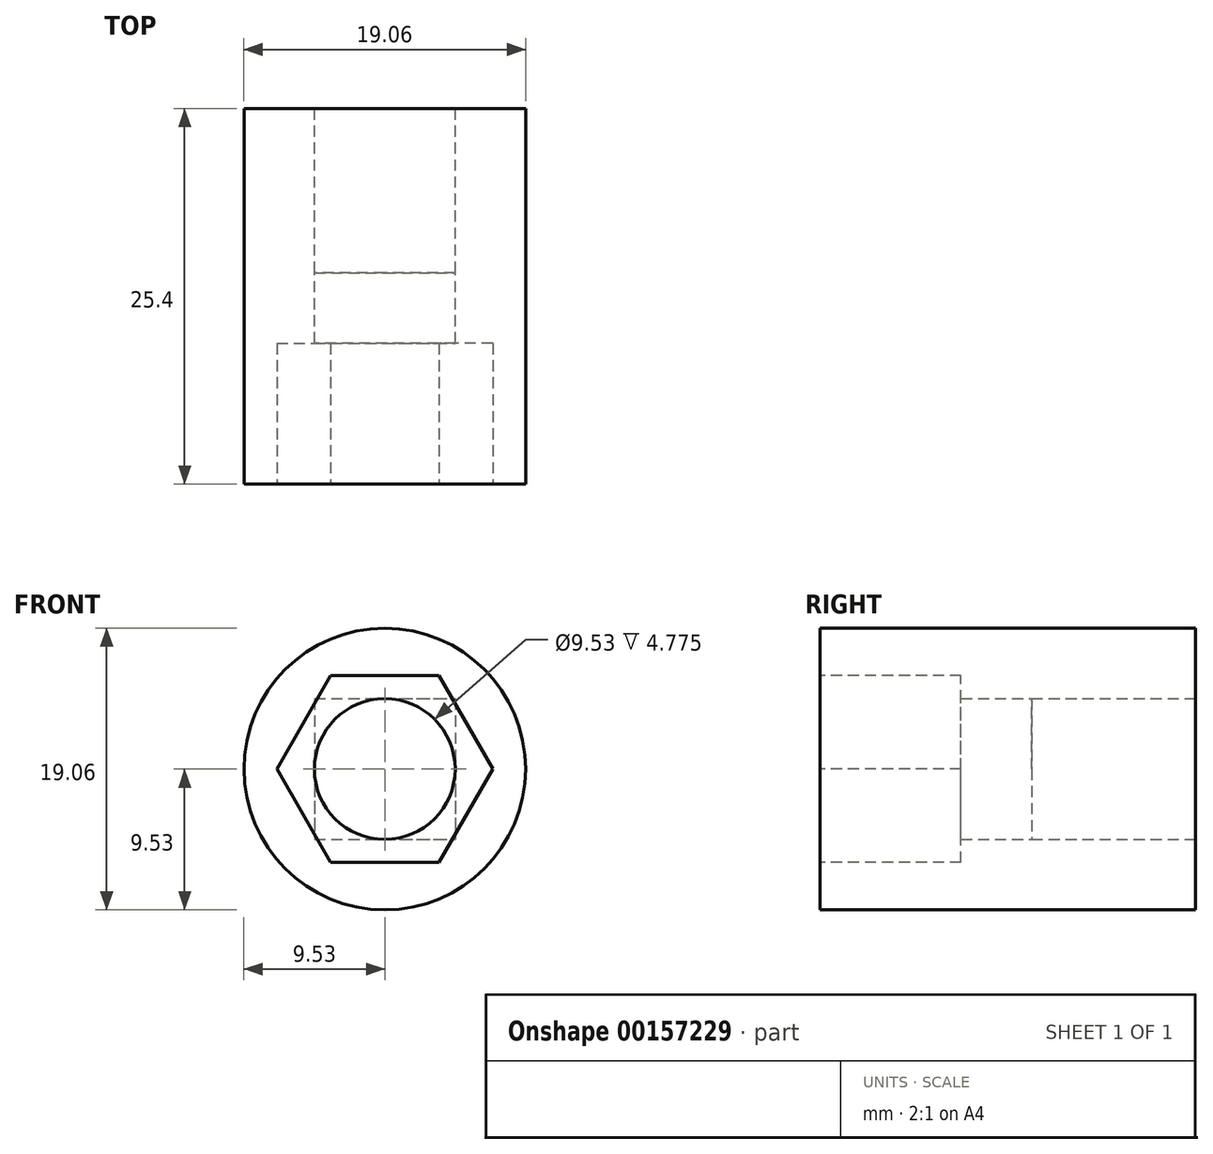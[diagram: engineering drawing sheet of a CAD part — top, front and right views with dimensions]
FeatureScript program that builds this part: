
annotation { "Feature Type Name" : "Feature", "Feature Type Description" : "" }
export const myFeature = defineFeature(function(context is Context, id is Id, definition is map)
    precondition{}
    {
        {
            var Q0;
            Q0=qCreatedBy(makeId("Front.planeOp"),FACE);
            var sketch = newSketch(context, id + "F0", { "sketchPlane" : qUnion([Q0])});
            skCircle(sketch, "E0", {"center": v(0, 0) * mm, "radius": 9.53 * mm});
            skSolve(sketch);
        }
        {
            var Q0;
            Q0 = qSketchRegion(id + "F0", true);
            extrude(context, id + "F1", {"entities" : qUnion([Q0]), "depth" : 25.4 * mm});
        }
        {
            var Q0;
            Q0=qCreatedBy(makeId("Front.planeOp"),FACE);
            var sketch = newSketch(context, id + "F2", { "sketchPlane" : qUnion([Q0])});
            skLineSegment(sketch, "E1.bottom", {"start": v(-4.76, 4.76) * mm, "end": v(4.76, 4.76) * mm});
            skLineSegment(sketch, "E1.top", {"start": v(-4.76, -4.76) * mm, "end": v(4.76, -4.76) * mm});
            skLineSegment(sketch, "E1.left", {"start": v(-4.76, 4.76) * mm, "end": v(-4.76, -4.76) * mm});
            skLineSegment(sketch, "E1.right", {"start": v(4.76, 4.76) * mm, "end": v(4.76, -4.76) * mm});
            skPoint(sketch, "E1.middle", {"position": v(0, 0) * mm});
            skCircle(sketch, "E2", {"center": v(0, 0) * mm, "radius": 4.76 * mm});
            skSolve(sketch);
        }
        {
            var Q0;
            {var subQ0=sQuery(id+"F2.wireOp",EDGE,"E2");var subQ1=makeQuery(id+"F2.imprint","INTERSECT",VERTEX,{"derivedFrom":[sQuery(id+"F2.wireOp",EDGE,"E1.bottom"),subQ0]});Q0=makeQuery(id+"F2.imprint","IMPRINT",FACE,{"disambiguationData":[TD([[makeQuery(id+"F2.imprint","IMPRINT",EDGE,{"disambiguationData":[TD([[subQ1,1.0]])],"derivedFrom":subQ0}),1.0]])]});}
            extrude(context, id + "F3", {"entities" : qUnion([Q0]), "operationType" : NewBodyOperationType.REMOVE, "endBound" : BoundingType.THROUGH_ALL, "depth" : 25.4 * mm});
        }
        {
            var Q0;
            Q0 = qSketchRegion(id + "F2", true);
            extrude(context, id + "F4", {"entities" : qUnion([Q0]), "operationType" : NewBodyOperationType.REMOVE, "depth" : 11.1 * mm});
        }
        {
            var Q0;
            Q0=makeQuery(id+"F1.opExtrude","CAP_FACE",FACE,{"disambiguationData":[OSD([sQuery(id+"F0.wireOp",EDGE,"E0")])],"isStart":false});
            var sketch = newSketch(context, id + "F5", { "sketchPlane" : qUnion([Q0])});
            skCircle(sketch, "E3.cCircle", {"center": v(0, 0) * mm, "radius": 6.32 * mm, "construction": true});
            skLineSegment(sketch, "E3.0", {"start": v(-3.65, 6.32) * mm, "end": v(3.65, 6.32) * mm});
            skLineSegment(sketch, "E3.1", {"start": v(3.65, 6.32) * mm, "end": v(7.3, 0) * mm});
            skLineSegment(sketch, "E3.2", {"start": v(7.3, 0) * mm, "end": v(3.65, -6.32) * mm});
            skLineSegment(sketch, "E3.3", {"start": v(3.65, -6.32) * mm, "end": v(-3.65, -6.32) * mm});
            skLineSegment(sketch, "E3.4", {"start": v(-3.65, -6.32) * mm, "end": v(-7.3, 0) * mm});
            skLineSegment(sketch, "E3.5", {"start": v(-7.3, 0) * mm, "end": v(-3.65, 6.32) * mm});
            skPoint(sketch, "E3.0.midPoint", {"position": v(0, 6.32) * mm});
            skSolve(sketch);
        }
        {
            var Q0;
            Q0=makeQuery(id+"F5.imprint","IMPRINT",FACE,{"disambiguationData":[TD([[makeQuery(id+"F5.imprint","IMPRINT",EDGE,{"derivedFrom":sQuery(id+"F5.wireOp",EDGE,"E3.0")}),-1.0]])]});
            extrude(context, id + "F6", {"entities" : qUnion([Q0]), "operationType" : NewBodyOperationType.REMOVE, "oppositeDirection" : true, "depth" : 9.52 * mm});
        }
    });
